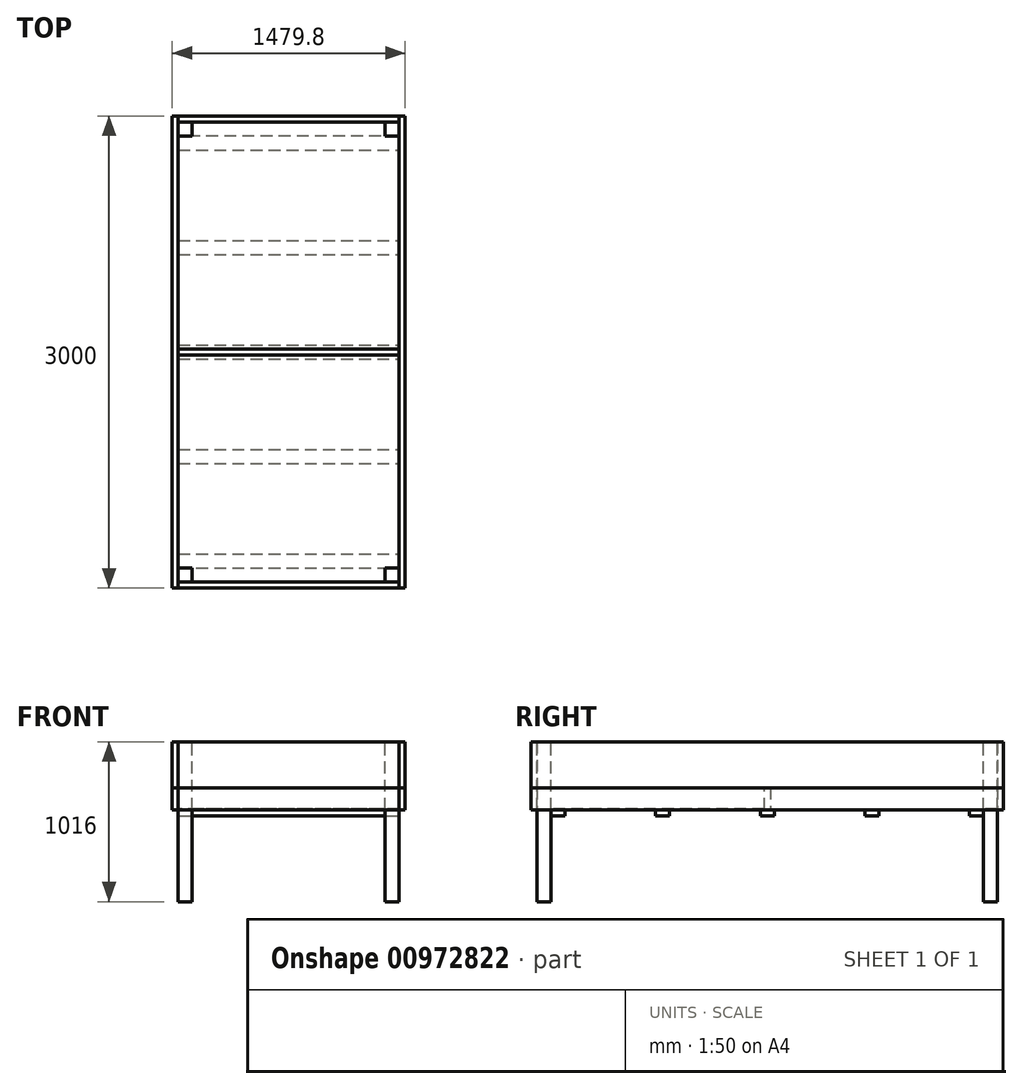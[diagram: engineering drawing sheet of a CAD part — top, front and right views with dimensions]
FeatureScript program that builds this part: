
annotation { "Feature Type Name" : "Feature", "Feature Type Description" : "" }
export const myFeature = defineFeature(function(context is Context, id is Id, definition is map)
    precondition{}
    {
        {
            var Q0;
            Q0=qCreatedBy(makeId("Top.planeOp"),FACE);
            var sketch = newSketch(context, id + "F0", { "sketchPlane" : qUnion([Q0])});
            skLineSegment(sketch, "E0.bottom", {"start": v(739.9, 1500) * mm, "end": v(-739.9, 1500) * mm});
            skLineSegment(sketch, "E0.top", {"start": v(739.9, -1500) * mm, "end": v(-739.9, -1500) * mm});
            skLineSegment(sketch, "E0.left", {"start": v(739.9, 1500) * mm, "end": v(739.9, -1500) * mm});
            skLineSegment(sketch, "E0.right", {"start": v(-739.9, 1500) * mm, "end": v(-739.9, -1500) * mm});
            skPoint(sketch, "E0.middle", {"position": v(0, 0) * mm});
            skSolve(sketch);
        }
        {
            var Q0;
            Q0=qCreatedBy(makeId("Front.planeOp"),FACE);
            var sketch = newSketch(context, id + "F1", { "sketchPlane" : qUnion([Q0])});
            skLineSegment(sketch, "E1.0", {"start": v(739.9, 0) * mm, "end": v(-739.9, 0) * mm});
            skLineSegment(sketch, "E2", {"start": v(-739.9, 0) * mm, "end": v(-739.9, -292.1) * mm});
            skLineSegment(sketch, "E3.MirrorCS", {"start": v(739.9, 0) * mm, "end": v(739.9, -292.1) * mm});
            skLineSegment(sketch, "E4", {"start": v(-739.9, -292.1) * mm, "end": v(739.9, -292.1) * mm});
            skLineSegment(sketch, "E5", {"start": v(0, 0) * mm, "end": v(0, -292.1) * mm, "construction": true});
            skLineSegment(sketch, "E6.0", {"start": v(-701.8, 0) * mm, "end": v(-701.8, -292.1) * mm});
            skLineSegment(sketch, "E7.0", {"start": v(701.8, 0) * mm, "end": v(701.8, -292.1) * mm});
            skLineSegment(sketch, "E8", {"start": v(0, 0) * mm, "end": v(0, -1016) * mm, "construction": true});
            skLineSegment(sketch, "E9", {"start": v(-739.9, -292.1) * mm, "end": v(0, -1016) * mm, "construction": true});
            skLineSegment(sketch, "E10", {"start": v(0, -1016) * mm, "end": v(-739.9, -1016) * mm, "construction": true});
            skLineSegment(sketch, "E11", {"start": v(-739.9, -1016) * mm, "end": v(-739.9, -292.1) * mm, "construction": true});
            skLineSegment(sketch, "E12", {"start": v(-739.9, -292.1) * mm, "end": v(-739.9, -431.8) * mm});
            skLineSegment(sketch, "E13", {"start": v(-739.9, -431.8) * mm, "end": v(-701.8, -431.8) * mm});
            skLineSegment(sketch, "E14", {"start": v(-701.8, -431.8) * mm, "end": v(-701.8, -292.1) * mm});
            skLineSegment(sketch, "E15.MirrorCS", {"start": v(739.9, -431.8) * mm, "end": v(701.8, -431.8) * mm});
            skLineSegment(sketch, "E16.MirrorCS", {"start": v(701.8, -431.8) * mm, "end": v(701.8, -292.1) * mm});
            skLineSegment(sketch, "E17.MirrorCS", {"start": v(739.9, -292.1) * mm, "end": v(739.9, -431.8) * mm});
            skSolve(sketch);
        }
        {
            var Q0;
            Q0=qCreatedBy(makeId("Front.planeOp"),FACE);
            var sketch = newSketch(context, id + "F2", { "sketchPlane" : qUnion([Q0])});
            skLineSegment(sketch, "E18.0", {"start": v(739.9, 0) * mm, "end": v(-739.9, 0) * mm, "construction": true});
            skLineSegment(sketch, "E19.0", {"start": v(-739.9, 0) * mm, "end": v(-739.9, -292.1) * mm, "construction": true});
            skLineSegment(sketch, "E20.0", {"start": v(-701.8, 0) * mm, "end": v(-701.8, -292.1) * mm, "construction": true});
            skLineSegment(sketch, "E21", {"start": v(-739.9, 0) * mm, "end": v(-739.9, 30) * mm});
            skLineSegment(sketch, "E22", {"start": v(-739.9, 30) * mm, "end": v(739.9, 30) * mm});
            skLineSegment(sketch, "E23", {"start": v(739.9, 30) * mm, "end": v(739.9, 0) * mm});
            skSolve(sketch);
        }
        {
            var Q0;
            {var subQ0=sQuery(id+"F1.wireOp",EDGE,"E2");Q0=makeQuery(id+"F1.imprint","IMPRINT",FACE,{"disambiguationData":[TD([[makeQuery(id+"F1.imprint","IMPRINT",EDGE,{"derivedFrom":subQ0}),1.0]])]});}
            var Q1;
            {var subQ0=sQuery(id+"F1.wireOp",EDGE,"E3.MirrorCS");Q1=makeQuery(id+"F1.imprint","IMPRINT",FACE,{"disambiguationData":[TD([[makeQuery(id+"F1.imprint","IMPRINT",EDGE,{"derivedFrom":subQ0}),-1.0]])]});}
            var Q2;
            Q2=sQuery(id+"F0.wireOp",VERTEX,"E0.top.end");
            var Q3;
            Q3=sQuery(id+"F0.wireOp",VERTEX,"E0.bottom.end");
            extrude(context, id + "F3", {"entities" : qUnion([Q0, Q1]), "endBound" : BoundingType.UP_TO_VERTEX, "depth" : 25 * mm, "endBoundEntityVertex" : qUnion([Q2]), "offsetDistance" : 25 * mm, "hasSecondDirection" : true, "secondDirectionBound" : SecondDirectionBoundingType.UP_TO_VERTEX, "secondDirectionOppositeDirection" : true, "secondDirectionDepth" : 25 * mm, "secondDirectionBoundEntityVertex" : qUnion([Q3])});
        }
        {
            var Q0;
            {var subQ0=sQuery(id+"F1.wireOp",EDGE,"E12");Q0=makeQuery(id+"F1.imprint","IMPRINT",FACE,{"disambiguationData":[TD([[makeQuery(id+"F1.imprint","IMPRINT",EDGE,{"derivedFrom":subQ0}),1.0]])]});}
            var Q1;
            Q1=makeQuery(id+"F1.imprint","IMPRINT",FACE,{"disambiguationData":[TD([[makeQuery(id+"F1.imprint","IMPRINT",EDGE,{"derivedFrom":sQuery(id+"F1.wireOp",EDGE,"E15.MirrorCS")}),-1.0]])]});
            var Q2;
            Q2=makeQuery(id+"F3.opExtrude","CAP_FACE",FACE,{"disambiguationData":[OSD([sQuery(id+"F1.wireOp",EDGE,"E1.0"),sQuery(id+"F1.wireOp",EDGE,"E2"),sQuery(id+"F1.wireOp",EDGE,"E4"),sQuery(id+"F1.wireOp",EDGE,"E6.0")])],"isStart":false});
            var Q3;
            Q3=makeQuery(id+"F3.opExtrude","CAP_FACE",FACE,{"disambiguationData":[OSD([sQuery(id+"F1.wireOp",EDGE,"E1.0"),sQuery(id+"F1.wireOp",EDGE,"E3.MirrorCS"),sQuery(id+"F1.wireOp",EDGE,"E4"),sQuery(id+"F1.wireOp",EDGE,"E7.0")])],"isStart":true});
            extrude(context, id + "F4", {"entities" : qUnion([Q0, Q1]), "endBound" : BoundingType.UP_TO_SURFACE, "depth" : 25 * mm, "endBoundEntityFace" : qUnion([Q2]), "offsetDistance" : 25 * mm, "hasSecondDirection" : true, "secondDirectionBound" : SecondDirectionBoundingType.UP_TO_SURFACE, "secondDirectionOppositeDirection" : true, "secondDirectionDepth" : 25 * mm, "secondDirectionBoundEntityFace" : qUnion([Q3])});
        }
        {
            var Q0;
            Q0=qCreatedBy(makeId("Right.planeOp"),FACE);
            var sketch = newSketch(context, id + "F5", { "sketchPlane" : qUnion([Q0])});
            skLineSegment(sketch, "E24", {"start": v(-1500, 0) * mm, "end": v(-1461.9, 0) * mm});
            skLineSegment(sketch, "E25", {"start": v(-1461.9, 0) * mm, "end": v(-1461.9, -292.1) * mm});
            skLineSegment(sketch, "E26", {"start": v(-1500, 0) * mm, "end": v(-1500, -292.1) * mm});
            skLineSegment(sketch, "E27", {"start": v(-1500, -292.1) * mm, "end": v(-1461.9, -292.1) * mm});
            skLineSegment(sketch, "E28.MirrorCS", {"start": v(1500, 0) * mm, "end": v(1461.9, 0) * mm});
            skLineSegment(sketch, "E29.MirrorCS", {"start": v(1500, -292.1) * mm, "end": v(1461.9, -292.1) * mm});
            skLineSegment(sketch, "E30.MirrorCS", {"start": v(1500, 0) * mm, "end": v(1500, -292.1) * mm});
            skLineSegment(sketch, "E31.MirrorCS", {"start": v(1461.9, 0) * mm, "end": v(1461.9, -292.1) * mm});
            skLineSegment(sketch, "E32", {"start": v(-1500, -292.1) * mm, "end": v(-1500, -431.8) * mm});
            skLineSegment(sketch, "E33", {"start": v(-1500, -431.8) * mm, "end": v(-1461.9, -431.8) * mm});
            skLineSegment(sketch, "E34", {"start": v(-1461.9, -431.8) * mm, "end": v(-1461.9, -292.1) * mm});
            skLineSegment(sketch, "E35.MirrorCS", {"start": v(1500, -431.8) * mm, "end": v(1461.9, -431.8) * mm});
            skLineSegment(sketch, "E36.MirrorCS", {"start": v(1461.9, -431.8) * mm, "end": v(1461.9, -292.1) * mm});
            skLineSegment(sketch, "E37.MirrorCS", {"start": v(1500, -292.1) * mm, "end": v(1500, -431.8) * mm});
            skLineSegment(sketch, "E38.0", {"start": v(-1500, -292.1) * mm, "end": v(1500, -292.1) * mm, "construction": true});
            skLineSegment(sketch, "E39.0", {"start": v(-1500, -431.8) * mm, "end": v(1500, -431.8) * mm, "construction": true});
            skLineSegment(sketch, "E40.0", {"start": v(0, -292.1) * mm, "end": v(0, -431.8) * mm, "construction": true});
            skLineSegment(sketch, "E41", {"start": v(0, -292.1) * mm, "end": v(-19.05, -292.1) * mm});
            skLineSegment(sketch, "E42", {"start": v(-19.05, -292.1) * mm, "end": v(-19.05, -431.8) * mm});
            skLineSegment(sketch, "E43", {"start": v(-19.05, -431.8) * mm, "end": v(19.05, -431.8) * mm});
            skLineSegment(sketch, "E44", {"start": v(19.05, -431.8) * mm, "end": v(19.05, -292.1) * mm});
            skLineSegment(sketch, "E45", {"start": v(19.05, -292.1) * mm, "end": v(0, -292.1) * mm});
            skSolve(sketch);
        }
        {
            var Q0;
            Q0=makeQuery(id+"F5.imprint","IMPRINT",FACE,{"disambiguationData":[TD([[makeQuery(id+"F5.imprint","IMPRINT",EDGE,{"derivedFrom":sQuery(id+"F5.wireOp",EDGE,"E28.MirrorCS")}),1.0]])]});
            var Q1;
            Q1=makeQuery(id+"F5.imprint","IMPRINT",FACE,{"disambiguationData":[TD([[makeQuery(id+"F5.imprint","IMPRINT",EDGE,{"derivedFrom":sQuery(id+"F5.wireOp",EDGE,"E24")}),-1.0]])]});
            var Q2;
            Q2=makeQuery(id+"F3.opExtrude","SWEPT_FACE",FACE,{"disambiguationData":[OSD([sQuery(id+"F1.wireOp",EDGE,"E7.0")])]});
            var Q3;
            Q3=makeQuery(id+"F3.opExtrude","SWEPT_FACE",FACE,{"disambiguationData":[OSD([sQuery(id+"F1.wireOp",EDGE,"E6.0")])]});
            extrude(context, id + "F6", {"entities" : qUnion([Q0, Q1]), "endBound" : BoundingType.UP_TO_SURFACE, "depth" : 25 * mm, "endBoundEntityFace" : qUnion([Q2]), "offsetDistance" : 25 * mm, "hasSecondDirection" : true, "secondDirectionBound" : SecondDirectionBoundingType.UP_TO_SURFACE, "secondDirectionOppositeDirection" : true, "secondDirectionDepth" : 25 * mm, "secondDirectionBoundEntityFace" : qUnion([Q3])});
        }
        {
            var Q0;
            Q0=makeQuery(id+"F5.imprint","IMPRINT",FACE,{"disambiguationData":[TD([[makeQuery(id+"F5.imprint","IMPRINT",EDGE,{"derivedFrom":sQuery(id+"F5.wireOp",EDGE,"E27")}),-1.0]])]});
            var Q1;
            Q1=makeQuery(id+"F5.imprint","IMPRINT",FACE,{"disambiguationData":[TD([[makeQuery(id+"F5.imprint","IMPRINT",EDGE,{"derivedFrom":sQuery(id+"F5.wireOp",EDGE,"E29.MirrorCS")}),1.0]])]});
            var Q2;
            Q2=makeQuery(id+"F5.imprint","IMPRINT",FACE,{"disambiguationData":[TD([[makeQuery(id+"F5.imprint","IMPRINT",EDGE,{"derivedFrom":sQuery(id+"F5.wireOp",EDGE,"E41")}),1.0]])]});
            var Q3;
            Q3=makeQuery(id+"F4.opExtrude","SWEPT_FACE",FACE,{"disambiguationData":[OSD([sQuery(id+"F1.wireOp",EDGE,"E16.MirrorCS")])]});
            var Q4;
            Q4=makeQuery(id+"F4.opExtrude","SWEPT_FACE",FACE,{"disambiguationData":[OSD([sQuery(id+"F1.wireOp",EDGE,"E14")])]});
            extrude(context, id + "F7", {"entities" : qUnion([Q0, Q1, Q2]), "endBound" : BoundingType.UP_TO_SURFACE, "depth" : 25 * mm, "endBoundEntityFace" : qUnion([Q3]), "offsetDistance" : 25 * mm, "hasSecondDirection" : true, "secondDirectionBound" : SecondDirectionBoundingType.UP_TO_SURFACE, "secondDirectionOppositeDirection" : true, "secondDirectionDepth" : 25 * mm, "secondDirectionBoundEntityFace" : qUnion([Q4])});
        }
        {
            var Q0;
            Q0=qCreatedBy(makeId("Top.planeOp"),FACE);
            var sketch = newSketch(context, id + "F8", { "sketchPlane" : qUnion([Q0])});
            skLineSegment(sketch, "E46.0", {"start": v(-701.8, -1500) * mm, "end": v(-701.8, 1500) * mm});
            skLineSegment(sketch, "E47.0", {"start": v(701.8, 1461.9) * mm, "end": v(-701.8, 1461.9) * mm});
            skLineSegment(sketch, "E48.0", {"start": v(-739.9, 0) * mm, "end": v(739.9, 0) * mm});
            skLineSegment(sketch, "E49", {"start": v(0, 0) * mm, "end": v(0, 1461.9) * mm, "construction": true});
            skLineSegment(sketch, "E50.bottom", {"start": v(-701.8, 1461.9) * mm, "end": v(-612.9, 1461.9) * mm});
            skLineSegment(sketch, "E50.top", {"start": v(-701.8, 1373) * mm, "end": v(-612.9, 1373) * mm});
            skLineSegment(sketch, "E50.left", {"start": v(-701.8, 1461.9) * mm, "end": v(-701.8, 1373) * mm});
            skLineSegment(sketch, "E50.right", {"start": v(-612.9, 1461.9) * mm, "end": v(-612.9, 1373) * mm});
            skLineSegment(sketch, "E51.MirrorCS", {"start": v(701.8, 1373) * mm, "end": v(612.9, 1373) * mm});
            skLineSegment(sketch, "E52.MirrorCS", {"start": v(701.8, 1461.9) * mm, "end": v(612.9, 1461.9) * mm});
            skLineSegment(sketch, "E53.MirrorCS", {"start": v(612.9, 1461.9) * mm, "end": v(612.9, 1373) * mm});
            skLineSegment(sketch, "E54.MirrorCS", {"start": v(701.8, 1461.9) * mm, "end": v(701.8, 1373) * mm});
            skLineSegment(sketch, "E55.MirrorCS", {"start": v(612.9, -1461.9) * mm, "end": v(612.9, -1373) * mm});
            skLineSegment(sketch, "E56.MirrorCS", {"start": v(701.8, -1461.9) * mm, "end": v(701.8, -1373) * mm});
            skLineSegment(sketch, "E57.MirrorCS", {"start": v(701.8, -1461.9) * mm, "end": v(612.9, -1461.9) * mm});
            skLineSegment(sketch, "E58.MirrorCS", {"start": v(701.8, -1373) * mm, "end": v(612.9, -1373) * mm});
            skLineSegment(sketch, "E59.MirrorCS", {"start": v(-612.9, -1461.9) * mm, "end": v(-612.9, -1373) * mm});
            skLineSegment(sketch, "E60.MirrorCS", {"start": v(-701.8, -1461.9) * mm, "end": v(-701.8, -1373) * mm});
            skLineSegment(sketch, "E61.MirrorCS", {"start": v(-701.8, -1373) * mm, "end": v(-612.9, -1373) * mm});
            skLineSegment(sketch, "E62.MirrorCS", {"start": v(-701.8, -1461.9) * mm, "end": v(-612.9, -1461.9) * mm});
            skSolve(sketch);
        }
        {
            var Q0;
            Q0=sQuery(id+"F1.wireOp",EDGE,"E10");
            cPlane(context, id + "F9", {"entities" : qUnion([Q0]), "cplaneType" : CPlaneType.LINE_ANGLE, "offset" : 25 * mm, "angle" : 90 * degree, "width" : 150 * mm, "height" : 150 * mm});
        }
        {
            var Q0;
            Q0=makeQuery(id+"F8.imprint","IMPRINT",FACE,{"disambiguationData":[TD([[makeQuery(id+"F8.imprint","IMPRINT",EDGE,{"derivedFrom":sQuery(id+"F8.wireOp",EDGE,"E50.bottom")}),-1.0]])]});
            var Q1;
            Q1=makeQuery(id+"F8.imprint","IMPRINT",FACE,{"disambiguationData":[TD([[makeQuery(id+"F8.imprint","IMPRINT",EDGE,{"derivedFrom":sQuery(id+"F8.wireOp",EDGE,"E51.MirrorCS")}),-1.0]])]});
            var Q2;
            Q2=makeQuery(id+"F8.imprint","IMPRINT",FACE,{"disambiguationData":[TD([[makeQuery(id+"F8.imprint","IMPRINT",EDGE,{"derivedFrom":sQuery(id+"F8.wireOp",EDGE,"E59.MirrorCS")}),1.0]])]});
            var Q3;
            Q3=makeQuery(id+"F8.imprint","IMPRINT",FACE,{"disambiguationData":[TD([[makeQuery(id+"F8.imprint","IMPRINT",EDGE,{"derivedFrom":sQuery(id+"F8.wireOp",EDGE,"E55.MirrorCS")}),-1.0]])]});
            var Q4;
            Q4=qCreatedBy(id+"F9.planeOp",FACE);
            extrude(context, id + "F10", {"entities" : qUnion([Q0, Q1, Q2, Q3]), "endBound" : BoundingType.UP_TO_SURFACE, "oppositeDirection" : true, "depth" : 40 * mm, "endBoundEntityFace" : qUnion([Q4]), "offsetDistance" : 25 * mm});
        }
        {
            var Q0;
            Q0=makeQuery(id+"F7.opExtrude","SWEPT_FACE",FACE,{"disambiguationData":[OSD([sQuery(id+"F5.wireOp",EDGE,"E33")])]});
            cPlane(context, id + "F11", {"entities" : qUnion([Q0]), "cplaneType" : CPlaneType.OFFSET, "offset" : 0 * mm, "width" : 152.4 * mm, "height" : 152.4 * mm});
        }
        {
            var Q0;
            Q0=qCreatedBy(id+"F11.planeOp",FACE);
            var sketch = newSketch(context, id + "F12", { "sketchPlane" : qUnion([Q0])});
            skLineSegment(sketch, "E63.0.0", {"start": v(-612.9, 1373) * mm, "end": v(-612.9, 1461.9) * mm});
            skLineSegment(sketch, "E63.0.1", {"start": v(-612.9, 1461.9) * mm, "end": v(-701.8, 1461.9) * mm});
            skLineSegment(sketch, "E63.0.2", {"start": v(-701.8, 1461.9) * mm, "end": v(-701.8, 1373) * mm});
            skLineSegment(sketch, "E63.0.3", {"start": v(-701.8, 1373) * mm, "end": v(-612.9, 1373) * mm});
            skLineSegment(sketch, "E64.0.0", {"start": v(612.9, 1461.9) * mm, "end": v(612.9, 1373) * mm});
            skLineSegment(sketch, "E64.0.1", {"start": v(612.9, 1373) * mm, "end": v(701.8, 1373) * mm});
            skLineSegment(sketch, "E64.0.2", {"start": v(701.8, 1373) * mm, "end": v(701.8, 1461.9) * mm});
            skLineSegment(sketch, "E64.0.3", {"start": v(701.8, 1461.9) * mm, "end": v(612.9, 1461.9) * mm});
            skLineSegment(sketch, "E65.0.0", {"start": v(-612.9, -1461.9) * mm, "end": v(-612.9, -1373) * mm});
            skLineSegment(sketch, "E65.0.1", {"start": v(-612.9, -1373) * mm, "end": v(-701.8, -1373) * mm});
            skLineSegment(sketch, "E65.0.2", {"start": v(-701.8, -1373) * mm, "end": v(-701.8, -1461.9) * mm});
            skLineSegment(sketch, "E65.0.3", {"start": v(-701.8, -1461.9) * mm, "end": v(-612.9, -1461.9) * mm});
            skLineSegment(sketch, "E66.0.0", {"start": v(612.9, -1461.9) * mm, "end": v(701.8, -1461.9) * mm});
            skLineSegment(sketch, "E66.0.1", {"start": v(701.8, -1461.9) * mm, "end": v(701.8, -1373) * mm});
            skLineSegment(sketch, "E66.0.2", {"start": v(701.8, -1373) * mm, "end": v(612.9, -1373) * mm});
            skLineSegment(sketch, "E66.0.3", {"start": v(612.9, -1373) * mm, "end": v(612.9, -1461.9) * mm});
            skLineSegment(sketch, "E67.0", {"start": v(701.8, -1461.9) * mm, "end": v(-701.8, -1461.9) * mm});
            skLineSegment(sketch, "E68.0", {"start": v(-701.8, 1500) * mm, "end": v(-701.8, 1373) * mm});
            skLineSegment(sketch, "E69.0", {"start": v(701.8, 1500) * mm, "end": v(701.8, 1373) * mm});
            skLineSegment(sketch, "E70.0", {"start": v(701.8, 1461.9) * mm, "end": v(-701.8, 1461.9) * mm});
            skLineSegment(sketch, "E71.0", {"start": v(701.8, 19.05) * mm, "end": v(-701.8, 19.05) * mm});
            skLineSegment(sketch, "E72.0", {"start": v(701.8, -19.05) * mm, "end": v(-701.8, -19.05) * mm});
            skLineSegment(sketch, "E73", {"start": v(-701.8, -1373) * mm, "end": v(701.8, -1373) * mm});
            skLineSegment(sketch, "E74.0", {"start": v(-739.9, 1500) * mm, "end": v(-739.9, -1500) * mm});
            skLineSegment(sketch, "E75.0", {"start": v(739.9, 1500) * mm, "end": v(739.9, -1500) * mm});
            skLineSegment(sketch, "E76", {"start": v(-739.9, 1373) * mm, "end": v(-701.8, 1373) * mm, "construction": true});
            skLineSegment(sketch, "E77", {"start": v(701.8, 1373) * mm, "end": v(739.9, 1373) * mm, "construction": true});
            skLineSegment(sketch, "E78", {"start": v(701.8, -1373) * mm, "end": v(739.9, -1373) * mm, "construction": true});
            skLineSegment(sketch, "E79", {"start": v(-701.8, -1373) * mm, "end": v(-739.9, -1373) * mm, "construction": true});
            skLineSegment(sketch, "E80", {"start": v(-739.9, 1373) * mm, "end": v(739.9, 1373) * mm});
            skLineSegment(sketch, "E81", {"start": v(-739.9, 1373) * mm, "end": v(-739.9, 1284.1) * mm});
            skLineSegment(sketch, "E82", {"start": v(-739.9, 1284.1) * mm, "end": v(739.9, 1284.1) * mm});
            skLineSegment(sketch, "E83", {"start": v(739.9, 1284.1) * mm, "end": v(739.9, 1373) * mm});
            skLineSegment(sketch, "E84.trimOffspring", {"start": v(-701.8, 1284.1) * mm, "end": v(-701.8, 708.72) * mm});
            skLineSegment(sketch, "E85.trimOffspring", {"start": v(701.8, 1284.1) * mm, "end": v(701.8, 708.72) * mm});
            skLineSegment(sketch, "E86.MirrorCS", {"start": v(-739.9, -1373) * mm, "end": v(739.9, -1373) * mm});
            skLineSegment(sketch, "E87.MirrorCS", {"start": v(-739.9, -1284.1) * mm, "end": v(739.9, -1284.1) * mm});
            skLineSegment(sketch, "E88.MirrorCS", {"start": v(739.9, -1284.1) * mm, "end": v(739.9, -1373) * mm});
            skLineSegment(sketch, "E89.MirrorCS", {"start": v(-739.9, -1373) * mm, "end": v(-739.9, -1284.1) * mm});
            skLineSegment(sketch, "E90", {"start": v(0, 1373) * mm, "end": v(0, 1284.1) * mm, "construction": true});
            skLineSegment(sketch, "E91", {"start": v(-739.9, 44.45) * mm, "end": v(739.9, 44.45) * mm});
            skLineSegment(sketch, "E92", {"start": v(-739.9, 44.45) * mm, "end": v(-739.9, -44.45) * mm});
            skLineSegment(sketch, "E93", {"start": v(-739.9, -44.45) * mm, "end": v(739.9, -44.45) * mm});
            skLineSegment(sketch, "E94", {"start": v(739.9, -44.45) * mm, "end": v(739.9, 44.45) * mm});
            skLineSegment(sketch, "E95", {"start": v(0, 44.45) * mm, "end": v(0, -44.45) * mm, "construction": true});
            skLineSegment(sketch, "E96", {"start": v(0, 1328.55) * mm, "end": v(0, 0) * mm, "construction": true});
            skLineSegment(sketch, "E97", {"start": v(0, -1373) * mm, "end": v(0, -1284.1) * mm, "construction": true});
            skLineSegment(sketch, "E98", {"start": v(0, 0) * mm, "end": v(0, -1328.55) * mm, "construction": true});
            skLineSegment(sketch, "E99", {"start": v(-739.9, 708.72) * mm, "end": v(739.9, 708.72) * mm});
            skLineSegment(sketch, "E100", {"start": v(-739.9, 708.72) * mm, "end": v(-739.9, 619.82) * mm});
            skLineSegment(sketch, "E101", {"start": v(-739.9, 619.82) * mm, "end": v(739.9, 619.82) * mm});
            skLineSegment(sketch, "E102", {"start": v(739.9, 619.82) * mm, "end": v(739.9, 708.72) * mm});
            skLineSegment(sketch, "E103", {"start": v(0, 708.72) * mm, "end": v(0, 619.82) * mm, "construction": true});
            skLineSegment(sketch, "E104", {"start": v(-739.9, -619.82) * mm, "end": v(739.9, -619.82) * mm});
            skLineSegment(sketch, "E105", {"start": v(-739.9, -619.82) * mm, "end": v(-739.9, -708.72) * mm});
            skLineSegment(sketch, "E106", {"start": v(-739.9, -708.72) * mm, "end": v(739.9, -708.72) * mm});
            skLineSegment(sketch, "E107", {"start": v(739.9, -708.72) * mm, "end": v(739.9, -619.82) * mm});
            skLineSegment(sketch, "E108", {"start": v(0, -619.82) * mm, "end": v(0, -708.72) * mm, "construction": true});
            skLineSegment(sketch, "E109.trimOffspring", {"start": v(-701.8, 619.82) * mm, "end": v(-701.8, 44.45) * mm});
            skLineSegment(sketch, "E110.trimOffspring", {"start": v(701.8, 619.82) * mm, "end": v(701.8, 44.45) * mm});
            skLineSegment(sketch, "E111.trimOffspring", {"start": v(701.8, -708.72) * mm, "end": v(701.8, -1284.1) * mm});
            skLineSegment(sketch, "E112.trimOffspring", {"start": v(-701.8, -708.72) * mm, "end": v(-701.8, -1284.1) * mm});
            skLineSegment(sketch, "E113.trimOffspring", {"start": v(-701.8, -1373) * mm, "end": v(-701.8, -1500) * mm});
            skLineSegment(sketch, "E114.trimOffspring", {"start": v(701.8, -1373) * mm, "end": v(701.8, -1500) * mm});
            skLineSegment(sketch, "E115.trimOffspring", {"start": v(701.8, -44.45) * mm, "end": v(701.8, -619.82) * mm});
            skLineSegment(sketch, "E116.trimOffspring", {"start": v(-701.8, 19.05) * mm, "end": v(-701.8, -19.05) * mm});
            skLineSegment(sketch, "E117.trimOffspring", {"start": v(-701.8, -44.45) * mm, "end": v(-701.8, -619.82) * mm});
            skLineSegment(sketch, "E118", {"start": v(701.8, 19.05) * mm, "end": v(701.8, -19.05) * mm});
            skLineSegment(sketch, "E119", {"start": v(701.8, 1373) * mm, "end": v(701.8, 1284.1) * mm});
            skLineSegment(sketch, "E120", {"start": v(701.8, 708.72) * mm, "end": v(701.8, 619.82) * mm});
            skLineSegment(sketch, "E121", {"start": v(701.8, 44.45) * mm, "end": v(701.8, -44.45) * mm});
            skLineSegment(sketch, "E122", {"start": v(701.8, -619.82) * mm, "end": v(701.8, -708.72) * mm});
            skLineSegment(sketch, "E123", {"start": v(701.8, -1284.1) * mm, "end": v(701.8, -1373) * mm});
            skLineSegment(sketch, "E124", {"start": v(-701.8, -1373) * mm, "end": v(-701.8, -1284.1) * mm});
            skLineSegment(sketch, "E125", {"start": v(-701.8, -708.72) * mm, "end": v(-701.8, -619.82) * mm});
            skLineSegment(sketch, "E126", {"start": v(-701.8, -44.45) * mm, "end": v(-701.8, 44.45) * mm});
            skLineSegment(sketch, "E127", {"start": v(-701.8, 619.82) * mm, "end": v(-701.8, 708.72) * mm});
            skLineSegment(sketch, "E128", {"start": v(-701.8, 1284.1) * mm, "end": v(-701.8, 1373) * mm});
            skSolve(sketch);
        }
        {
            var Q0;
            {var subQ5=sQuery(id+"F12.wireOp",EDGE,"E63.0.0");Q0=makeQuery(id+"F12.imprint","IMPRINT",FACE,{"disambiguationData":[TD([[makeQuery(id+"F12.imprint","IMPRINT",EDGE,{"derivedFrom":subQ5}),-1.0]])]});}
            var Q1;
            {var subQ3=sQuery(id+"F12.wireOp",EDGE,"E65.0.0");Q1=makeQuery(id+"F12.imprint","IMPRINT",FACE,{"disambiguationData":[TD([[makeQuery(id+"F12.imprint","IMPRINT",EDGE,{"derivedFrom":subQ3}),-1.0]])]});}
            var Q2;
            {var subQ2=sQuery(id+"F12.wireOp",EDGE,"E119");Q2=makeQuery(id+"F12.imprint","IMPRINT",FACE,{"disambiguationData":[TD([[makeQuery(id+"F12.imprint","IMPRINT",EDGE,{"derivedFrom":subQ2}),-1.0]])]});}
            var Q3;
            {var subQ0=sQuery(id+"F12.wireOp",EDGE,"E84.trimOffspring");Q3=makeQuery(id+"F12.imprint","IMPRINT",FACE,{"disambiguationData":[TD([[makeQuery(id+"F12.imprint","IMPRINT",EDGE,{"derivedFrom":subQ0}),1.0]])]});}
            var Q4;
            {var subQ2=sQuery(id+"F12.wireOp",EDGE,"E120");Q4=makeQuery(id+"F12.imprint","IMPRINT",FACE,{"disambiguationData":[TD([[makeQuery(id+"F12.imprint","IMPRINT",EDGE,{"derivedFrom":subQ2}),-1.0]])]});}
            var Q5;
            {var subQ0=sQuery(id+"F12.wireOp",EDGE,"E109.trimOffspring");Q5=makeQuery(id+"F12.imprint","IMPRINT",FACE,{"disambiguationData":[TD([[makeQuery(id+"F12.imprint","IMPRINT",EDGE,{"derivedFrom":subQ0}),1.0]])]});}
            var Q6;
            {var subQ0=sQuery(id+"F12.wireOp",EDGE,"E71.0");Q6=makeQuery(id+"F12.imprint","IMPRINT",FACE,{"disambiguationData":[TD([[makeQuery(id+"F12.imprint","IMPRINT",EDGE,{"derivedFrom":subQ0}),-1.0]])]});}
            var Q7;
            {var subQ0=sQuery(id+"F12.wireOp",EDGE,"E115.trimOffspring");Q7=makeQuery(id+"F12.imprint","IMPRINT",FACE,{"disambiguationData":[TD([[makeQuery(id+"F12.imprint","IMPRINT",EDGE,{"derivedFrom":subQ0}),-1.0]])]});}
            var Q8;
            {var subQ2=sQuery(id+"F12.wireOp",EDGE,"E123");Q8=makeQuery(id+"F12.imprint","IMPRINT",FACE,{"disambiguationData":[TD([[makeQuery(id+"F12.imprint","IMPRINT",EDGE,{"derivedFrom":subQ2}),-1.0]])]});}
            var Q9;
            {var subQ0=sQuery(id+"F12.wireOp",EDGE,"E122");Q9=makeQuery(id+"F12.imprint","IMPRINT",FACE,{"disambiguationData":[TD([[makeQuery(id+"F12.imprint","IMPRINT",EDGE,{"derivedFrom":subQ0}),-1.0]])]});}
            var Q10;
            {var subQ0=sQuery(id+"F12.wireOp",EDGE,"E111.trimOffspring");Q10=makeQuery(id+"F12.imprint","IMPRINT",FACE,{"disambiguationData":[TD([[makeQuery(id+"F12.imprint","IMPRINT",EDGE,{"derivedFrom":subQ0}),-1.0]])]});}
            var Q11;
            {var subQ0=sQuery(id+"F12.wireOp",EDGE,"E72.0");Q11=makeQuery(id+"F12.imprint","IMPRINT",FACE,{"disambiguationData":[TD([[makeQuery(id+"F12.imprint","IMPRINT",EDGE,{"derivedFrom":subQ0}),1.0]])]});}
            extrude(context, id + "F13", {"entities" : qUnion([Q0, Q1, Q2, Q3, Q4, Q5, Q6, Q7, Q8, Q9, Q10, Q11]), "oppositeDirection" : true, "depth" : 6.35 * mm, "offsetDistance" : 25.4 * mm});
        }
        {
            var Q0;
            {var subQ5=sQuery(id+"F12.wireOp",EDGE,"E81");Q0=makeQuery(id+"F12.imprint","IMPRINT",FACE,{"disambiguationData":[TD([[makeQuery(id+"F12.imprint","IMPRINT",EDGE,{"derivedFrom":subQ5}),1.0]])]});}
            var Q1;
            {var subQ0=sQuery(id+"F12.wireOp",EDGE,"E100");Q1=makeQuery(id+"F12.imprint","IMPRINT",FACE,{"disambiguationData":[TD([[makeQuery(id+"F12.imprint","IMPRINT",EDGE,{"derivedFrom":subQ0}),1.0]])]});}
            var Q2;
            Q2=makeQuery(id+"F12.imprint","IMPRINT",FACE,{"disambiguationData":[TD([[makeQuery(id+"F12.imprint","IMPRINT",EDGE,{"derivedFrom":sQuery(id+"F12.wireOp",EDGE,"E71.0")}),-1.0]])]});
            var Q3;
            Q3=makeQuery(id+"F12.imprint","IMPRINT",FACE,{"disambiguationData":[TD([[makeQuery(id+"F12.imprint","IMPRINT",EDGE,{"derivedFrom":sQuery(id+"F12.wireOp",EDGE,"E71.0")}),1.0]])]});
            var Q4;
            {var subQ0=sQuery(id+"F12.wireOp",EDGE,"E105");Q4=makeQuery(id+"F12.imprint","IMPRINT",FACE,{"disambiguationData":[TD([[makeQuery(id+"F12.imprint","IMPRINT",EDGE,{"derivedFrom":subQ0}),1.0]])]});}
            var Q5;
            {var subQ6=sQuery(id+"F12.wireOp",EDGE,"E88.MirrorCS");Q5=makeQuery(id+"F12.imprint","IMPRINT",FACE,{"disambiguationData":[TD([[makeQuery(id+"F12.imprint","IMPRINT",EDGE,{"derivedFrom":subQ6}),-1.0]])]});}
            var Q6;
            {var subQ2=sQuery(id+"F12.wireOp",EDGE,"E119");Q6=makeQuery(id+"F12.imprint","IMPRINT",FACE,{"disambiguationData":[TD([[makeQuery(id+"F12.imprint","IMPRINT",EDGE,{"derivedFrom":subQ2}),-1.0]])]});}
            var Q7;
            {var subQ2=sQuery(id+"F12.wireOp",EDGE,"E120");Q7=makeQuery(id+"F12.imprint","IMPRINT",FACE,{"disambiguationData":[TD([[makeQuery(id+"F12.imprint","IMPRINT",EDGE,{"derivedFrom":subQ2}),-1.0]])]});}
            var Q8;
            {var subQ4=sQuery(id+"F12.wireOp",EDGE,"E92");Q8=makeQuery(id+"F12.imprint","IMPRINT",FACE,{"disambiguationData":[TD([[makeQuery(id+"F12.imprint","IMPRINT",EDGE,{"derivedFrom":subQ4}),1.0]])]});}
            var Q9;
            {var subQ0=sQuery(id+"F12.wireOp",EDGE,"E72.0");Q9=makeQuery(id+"F12.imprint","IMPRINT",FACE,{"disambiguationData":[TD([[makeQuery(id+"F12.imprint","IMPRINT",EDGE,{"derivedFrom":subQ0}),1.0]])]});}
            var Q10;
            {var subQ4=sQuery(id+"F12.wireOp",EDGE,"E94");Q10=makeQuery(id+"F12.imprint","IMPRINT",FACE,{"disambiguationData":[TD([[makeQuery(id+"F12.imprint","IMPRINT",EDGE,{"derivedFrom":subQ4}),1.0]])]});}
            var Q11;
            {var subQ2=sQuery(id+"F12.wireOp",EDGE,"E102");Q11=makeQuery(id+"F12.imprint","IMPRINT",FACE,{"disambiguationData":[TD([[makeQuery(id+"F12.imprint","IMPRINT",EDGE,{"derivedFrom":subQ2}),1.0]])]});}
            var Q12;
            {var subQ2=sQuery(id+"F12.wireOp",EDGE,"E83");Q12=makeQuery(id+"F12.imprint","IMPRINT",FACE,{"disambiguationData":[TD([[makeQuery(id+"F12.imprint","IMPRINT",EDGE,{"derivedFrom":subQ2}),1.0]])]});}
            var Q13;
            {var subQ0=sQuery(id+"F12.wireOp",EDGE,"E122");Q13=makeQuery(id+"F12.imprint","IMPRINT",FACE,{"disambiguationData":[TD([[makeQuery(id+"F12.imprint","IMPRINT",EDGE,{"derivedFrom":subQ0}),-1.0]])]});}
            var Q14;
            {var subQ0=sQuery(id+"F12.wireOp",EDGE,"E89.MirrorCS");Q14=makeQuery(id+"F12.imprint","IMPRINT",FACE,{"disambiguationData":[TD([[makeQuery(id+"F12.imprint","IMPRINT",EDGE,{"derivedFrom":subQ0}),-1.0]])]});}
            var Q15;
            {var subQ2=sQuery(id+"F12.wireOp",EDGE,"E123");Q15=makeQuery(id+"F12.imprint","IMPRINT",FACE,{"disambiguationData":[TD([[makeQuery(id+"F12.imprint","IMPRINT",EDGE,{"derivedFrom":subQ2}),-1.0]])]});}
            var Q16;
            {var subQ0=sQuery(id+"F12.wireOp",EDGE,"E107");Q16=makeQuery(id+"F12.imprint","IMPRINT",FACE,{"disambiguationData":[TD([[makeQuery(id+"F12.imprint","IMPRINT",EDGE,{"derivedFrom":subQ0}),1.0]])]});}
            extrude(context, id + "F14", {"entities" : qUnion([Q0, Q1, Q2, Q3, Q4, Q5, Q6, Q7, Q8, Q9, Q10, Q11, Q12, Q13, Q14, Q15, Q16]), "depth" : 38.1 * mm, "offsetDistance" : 25.4 * mm});
        }
    });
